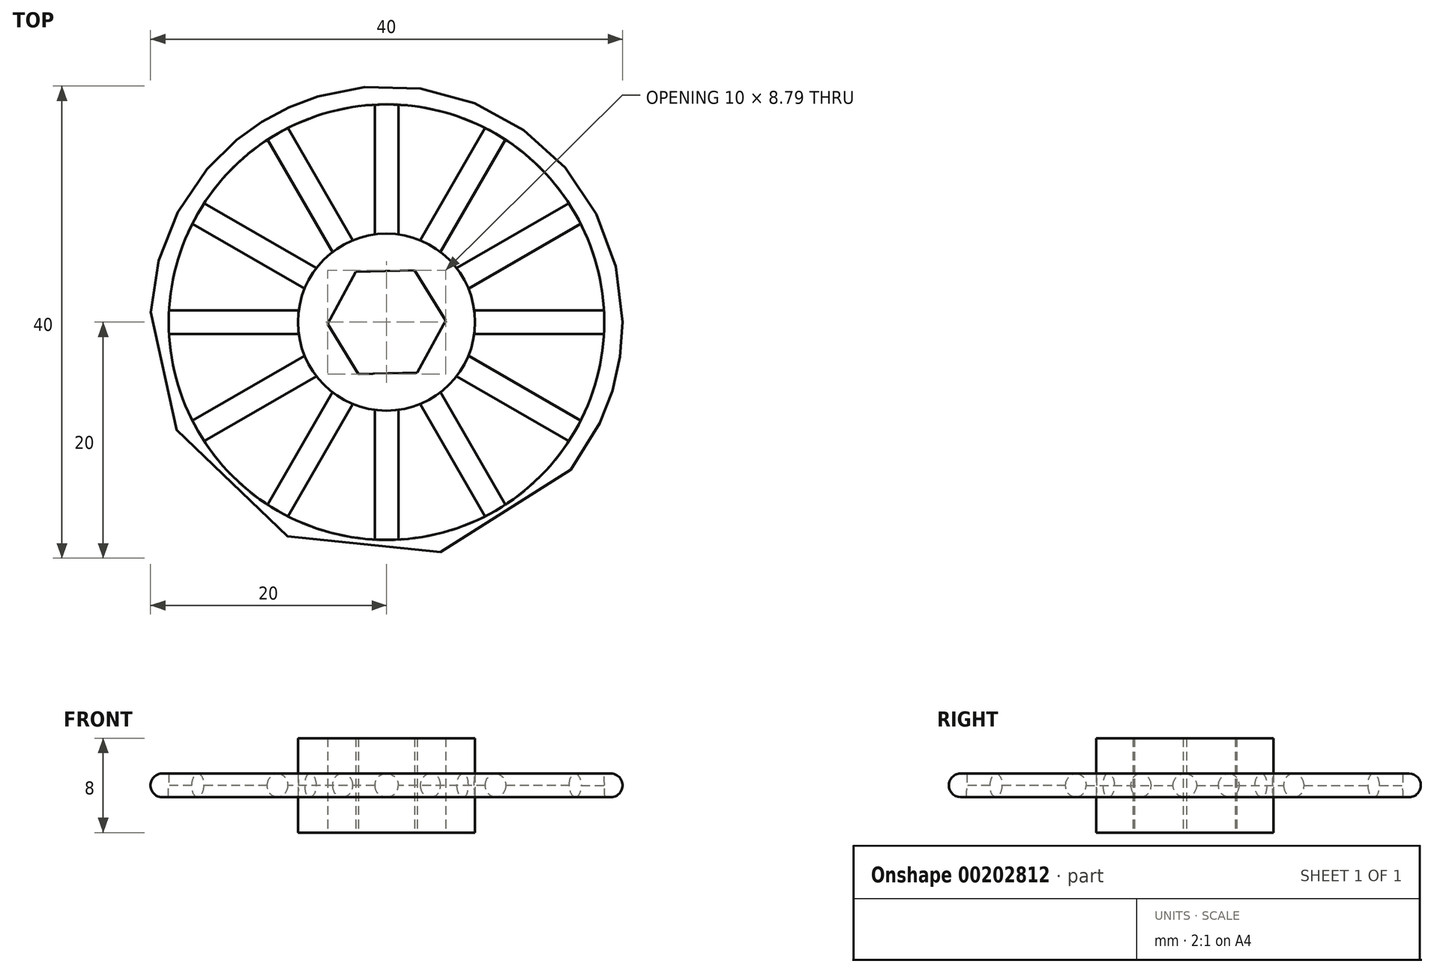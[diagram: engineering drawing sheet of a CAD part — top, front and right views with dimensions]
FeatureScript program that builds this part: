
annotation { "Feature Type Name" : "Feature", "Feature Type Description" : "" }
export const myFeature = defineFeature(function(context is Context, id is Id, definition is map)
    precondition{}
    {
        {
            var Q0;
            Q0=qCreatedBy(makeId("Top.planeOp"),FACE);
            var sketch = newSketch(context, id + "F0", { "sketchPlane" : qUnion([Q0])});
            skCircle(sketch, "E0", {"center": v(0, 0) * mm, "radius": 20 * mm});
            skCircle(sketch, "E1", {"center": v(0, 0) * mm, "radius": 5 * mm});
            skCircle(sketch, "E2", {"center": v(0, 0) * mm, "radius": 7.5 * mm});
            skCircle(sketch, "E3.cCircle", {"center": v(0, 0) * mm, "radius": 5 * mm, "construction": true});
            skLineSegment(sketch, "E3.0", {"start": v(2.61, -4.26) * mm, "end": v(-2.39, -4.4) * mm});
            skLineSegment(sketch, "E3.1", {"start": v(-2.39, -4.4) * mm, "end": v(-5, -0.13) * mm});
            skLineSegment(sketch, "E3.2", {"start": v(-5, -0.13) * mm, "end": v(-2.61, 4.26) * mm});
            skLineSegment(sketch, "E3.3", {"start": v(-2.61, 4.26) * mm, "end": v(2.39, 4.4) * mm});
            skLineSegment(sketch, "E3.4", {"start": v(2.39, 4.4) * mm, "end": v(5, 0.13) * mm});
            skLineSegment(sketch, "E3.5", {"start": v(5, 0.13) * mm, "end": v(2.61, -4.26) * mm});
            skCircle(sketch, "E4.0", {"center": v(0, 0) * mm, "radius": 18.5 * mm});
            skLineSegment(sketch, "E5.trimOffspring", {"start": v(7.5, 0) * mm, "end": v(18.5, 0) * mm, "construction": true});
            skLineSegment(sketch, "E6.0", {"start": v(7.43, -1) * mm, "end": v(18.47, -1) * mm});
            skLineSegment(sketch, "E7.0", {"start": v(7.43, 1) * mm, "end": v(18.47, 1) * mm});
            skSolve(sketch);
        }
        {
            var Q0;
            Q0=makeQuery(id+"F0.imprint","IMPRINT",FACE,{"disambiguationData":[TD([[makeQuery(id+"F0.imprint","IMPRINT",EDGE,{"derivedFrom":sQuery(id+"F0.wireOp",EDGE,"E2")}),1.0]])]});
            var Q1;
            {var subQ0=sQuery(id+"F0.wireOp",EDGE,"E3.1");Q1=makeQuery(id+"F0.imprint","IMPRINT",FACE,{"disambiguationData":[TD([[makeQuery(id+"F0.imprint","IMPRINT",EDGE,{"derivedFrom":subQ0}),1.0]])]});}
            var Q2;
            {var subQ0=sQuery(id+"F0.wireOp",EDGE,"E3.2");Q2=makeQuery(id+"F0.imprint","IMPRINT",FACE,{"disambiguationData":[TD([[makeQuery(id+"F0.imprint","IMPRINT",EDGE,{"derivedFrom":subQ0}),1.0]])]});}
            var Q3;
            {var subQ0=sQuery(id+"F0.wireOp",EDGE,"E3.3");Q3=makeQuery(id+"F0.imprint","IMPRINT",FACE,{"disambiguationData":[TD([[makeQuery(id+"F0.imprint","IMPRINT",EDGE,{"derivedFrom":subQ0}),1.0]])]});}
            var Q4;
            {var subQ0=sQuery(id+"F0.wireOp",EDGE,"E3.4");Q4=makeQuery(id+"F0.imprint","IMPRINT",FACE,{"disambiguationData":[TD([[makeQuery(id+"F0.imprint","IMPRINT",EDGE,{"derivedFrom":subQ0}),1.0]])]});}
            var Q5;
            {var subQ0=sQuery(id+"F0.wireOp",EDGE,"E3.5");Q5=makeQuery(id+"F0.imprint","IMPRINT",FACE,{"disambiguationData":[TD([[makeQuery(id+"F0.imprint","IMPRINT",EDGE,{"derivedFrom":subQ0}),1.0]])]});}
            var Q6;
            {var subQ0=sQuery(id+"F0.wireOp",EDGE,"E3.0");Q6=makeQuery(id+"F0.imprint","IMPRINT",FACE,{"disambiguationData":[TD([[makeQuery(id+"F0.imprint","IMPRINT",EDGE,{"derivedFrom":subQ0}),1.0]])]});}
            extrude(context, id + "F1", {"entities" : qUnion([Q0, Q1, Q2, Q3, Q4, Q5, Q6]), "depth" : 4 * mm, "hasSecondDirection" : true, "secondDirectionOppositeDirection" : true, "secondDirectionDepth" : 4 * mm});
        }
        {
            var Q0;
            {var subQ0=sQuery(id+"F0.wireOp",EDGE,"E6.0");Q0=makeQuery(id+"F0.imprint","IMPRINT",FACE,{"disambiguationData":[TD([[makeQuery(id+"F0.imprint","IMPRINT",EDGE,{"derivedFrom":subQ0}),1.0]])]});}
            extrude(context, id + "F2", {"entities" : qUnion([Q0]), "depth" : 1 * mm, "hasSecondDirection" : true, "secondDirectionOppositeDirection" : true, "secondDirectionDepth" : 1 * mm});
        }
        {
            var Q0;
            Q0=qCreatedBy(makeId("Right.planeOp"),FACE);
            var sketch = newSketch(context, id + "F3", { "sketchPlane" : qUnion([Q0])});
            skLineSegment(sketch, "E8", {"start": v(0, -29.36) * mm, "end": v(0, 29.36) * mm, "construction": true});
            skSolve(sketch);
        }
        {
            var Q0;
            Q0=makeQuery(id+"F2.opExtrude","CAP_EDGE",EDGE,{"disambiguationData":[OSD([sQuery(id+"F0.wireOp",EDGE,"E6.0")])],"isStart":false});
            var Q1;
            Q1=makeQuery(id+"F2.opExtrude","CAP_EDGE",EDGE,{"disambiguationData":[OSD([sQuery(id+"F0.wireOp",EDGE,"E7.0")])],"isStart":false});
            var Q2;
            Q2=makeQuery(id+"F2.opExtrude","CAP_EDGE",EDGE,{"disambiguationData":[OSD([sQuery(id+"F0.wireOp",EDGE,"E6.0")])],"isStart":true});
            var Q3;
            Q3=makeQuery(id+"F2.opExtrude","CAP_EDGE",EDGE,{"disambiguationData":[OSD([sQuery(id+"F0.wireOp",EDGE,"E7.0")])],"isStart":true});
            fillet(context, id + "F4", {"entities" : qUnion([Q0, Q1, Q2, Q3]), "radius" : 1 * mm, "tangentPropagation" : true, "allowEdgeOverflow" : false});
        }
        {
            var Q0;
            Q0=makeQuery(id+"F2.opExtrude","SWEPT_BODY",BODY,{"disambiguationData":[OSD([sQuery(id+"F0.wireOp",EDGE,"E2"),sQuery(id+"F0.wireOp",EDGE,"E4.0"),sQuery(id+"F0.wireOp",EDGE,"E6.0"),sQuery(id+"F0.wireOp",EDGE,"E7.0")])]});
            var Q1;
            Q1=sQuery(id+"F3.wireOp",EDGE,"E8");
            circularPattern(context, id + "F5", {"entities" : qUnion([Q0]), "axis" : qUnion([Q1]), "angle" : 360 * degree, "instanceCount" : 12, "equalSpace" : true});
        }
        {
            var Q0;
            Q0=makeQuery(id+"F0.imprint","IMPRINT",FACE,{"disambiguationData":[TD([[makeQuery(id+"F0.imprint","IMPRINT",EDGE,{"derivedFrom":sQuery(id+"F0.wireOp",EDGE,"E0")}),1.0]])]});
            extrude(context, id + "F6", {"entities" : qUnion([Q0]), "operationType" : NewBodyOperationType.ADD, "depth" : 1 * mm, "hasDraft" : true, "draftAngle" : 3 * degree, "hasSecondDirection" : true, "secondDirectionOppositeDirection" : true, "secondDirectionDepth" : 1 * mm});
        }
        {
            var Q0;
            Q0=makeQuery(id+"F6.opExtrude","CAP_EDGE",EDGE,{"disambiguationData":[OSD([sQuery(id+"F0.wireOp",EDGE,"E0")])],"isStart":false});
            var Q1;
            Q1=makeQuery(id+"F6.opExtrude","CAP_EDGE",EDGE,{"disambiguationData":[OSD([sQuery(id+"F0.wireOp",EDGE,"E0")])],"isStart":true});
            fillet(context, id + "F7", {"entities" : qUnion([Q0, Q1]), "radius" : 1 * mm, "tangentPropagation" : true, "allowEdgeOverflow" : false});
        }
    });
